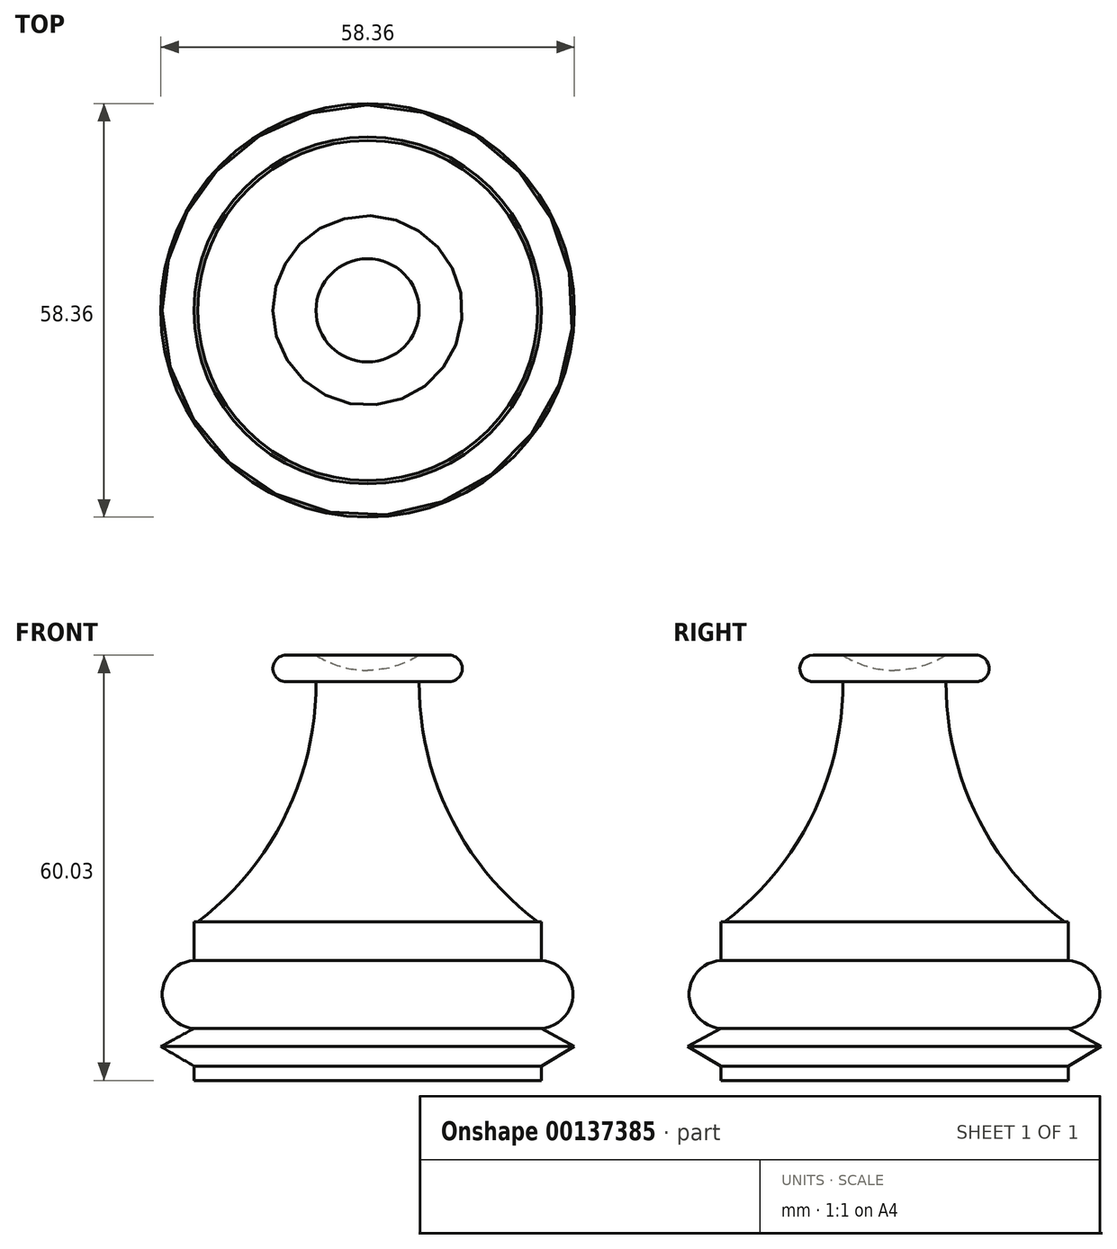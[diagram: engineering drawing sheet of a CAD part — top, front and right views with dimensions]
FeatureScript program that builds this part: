
annotation { "Feature Type Name" : "Feature", "Feature Type Description" : "" }
export const myFeature = defineFeature(function(context is Context, id is Id, definition is map)
    precondition{}
    {
        {
            var Q0;
            Q0=qCreatedBy(makeId("Front.planeOp"),FACE);
            var sketch = newSketch(context, id + "F0", { "sketchPlane" : qUnion([Q0])});
            skLineSegment(sketch, "E0", {"start": v(0, 0) * mm, "end": v(24.5, 0) * mm});
            skLineSegment(sketch, "E1", {"start": v(24.5, 0) * mm, "end": v(24.5, 2.02) * mm});
            skLineSegment(sketch, "E2", {"start": v(24.5, 2.02) * mm, "end": v(29.18, 4.78) * mm});
            skLineSegment(sketch, "E3", {"start": v(29.18, 4.78) * mm, "end": v(24.5, 7.34) * mm});
            skArc(sketch, "E4", {"start": v(24.5, 7.34) * mm, "mid": v(28.99, 12.15) * mm, "end": v(24.5, 16.95) * mm});
            skLineSegment(sketch, "E5", {"start": v(24.5, 16.95) * mm, "end": v(24.5, 22.37) * mm});
            skLineSegment(sketch, "E6", {"start": v(24.5, 22.37) * mm, "end": v(24, 22.37) * mm});
            skArc(sketch, "E7", {"start": v(7.28, 56.3) * mm, "mid": v(11.62, 37.35) * mm, "end": v(24, 22.37) * mm});
            skLineSegment(sketch, "E8", {"start": v(7.28, 56.3) * mm, "end": v(11.5, 56.3) * mm});
            skArc(sketch, "E9", {"start": v(11.5, 56.3) * mm, "mid": v(13.36, 58.16) * mm, "end": v(11.5, 60.03) * mm});
            skLineSegment(sketch, "E10", {"start": v(11.5, 60.03) * mm, "end": v(7.28, 60.03) * mm});
            skLineSegment(sketch, "E11", {"start": v(0, 0) * mm, "end": v(0, 81.14) * mm});
            skArc(sketch, "E12", {"start": v(7.28, 60.03) * mm, "mid": v(12.95, 75.19) * mm, "end": v(0, 84.89) * mm});
            skLineSegment(sketch, "E13", {"start": v(0, 81.14) * mm, "end": v(0, 84.89) * mm});
            skLineSegment(sketch, "E14", {"start": v(0, 84.89) * mm, "end": v(56.56, 84.9) * mm, "construction": true});
            skSolve(sketch);
        }
        {
            var Q0;
            Q0=makeQuery(id+"F0.imprint","IMPRINT",FACE,{"disambiguationData":[TD([[makeQuery(id+"F0.imprint","IMPRINT",EDGE,{"derivedFrom":sQuery(id+"F0.wireOp",EDGE,"E0")}),1.0]])]});
            var Q1;
            Q1=sQuery(id+"F0.wireOp",EDGE,"E13");
            revolve(context, id + "F1", {"entities" : qUnion([Q0]), "axis" : qUnion([Q1]), "revolveType" : RevolveType.FULL});
        }
    });
